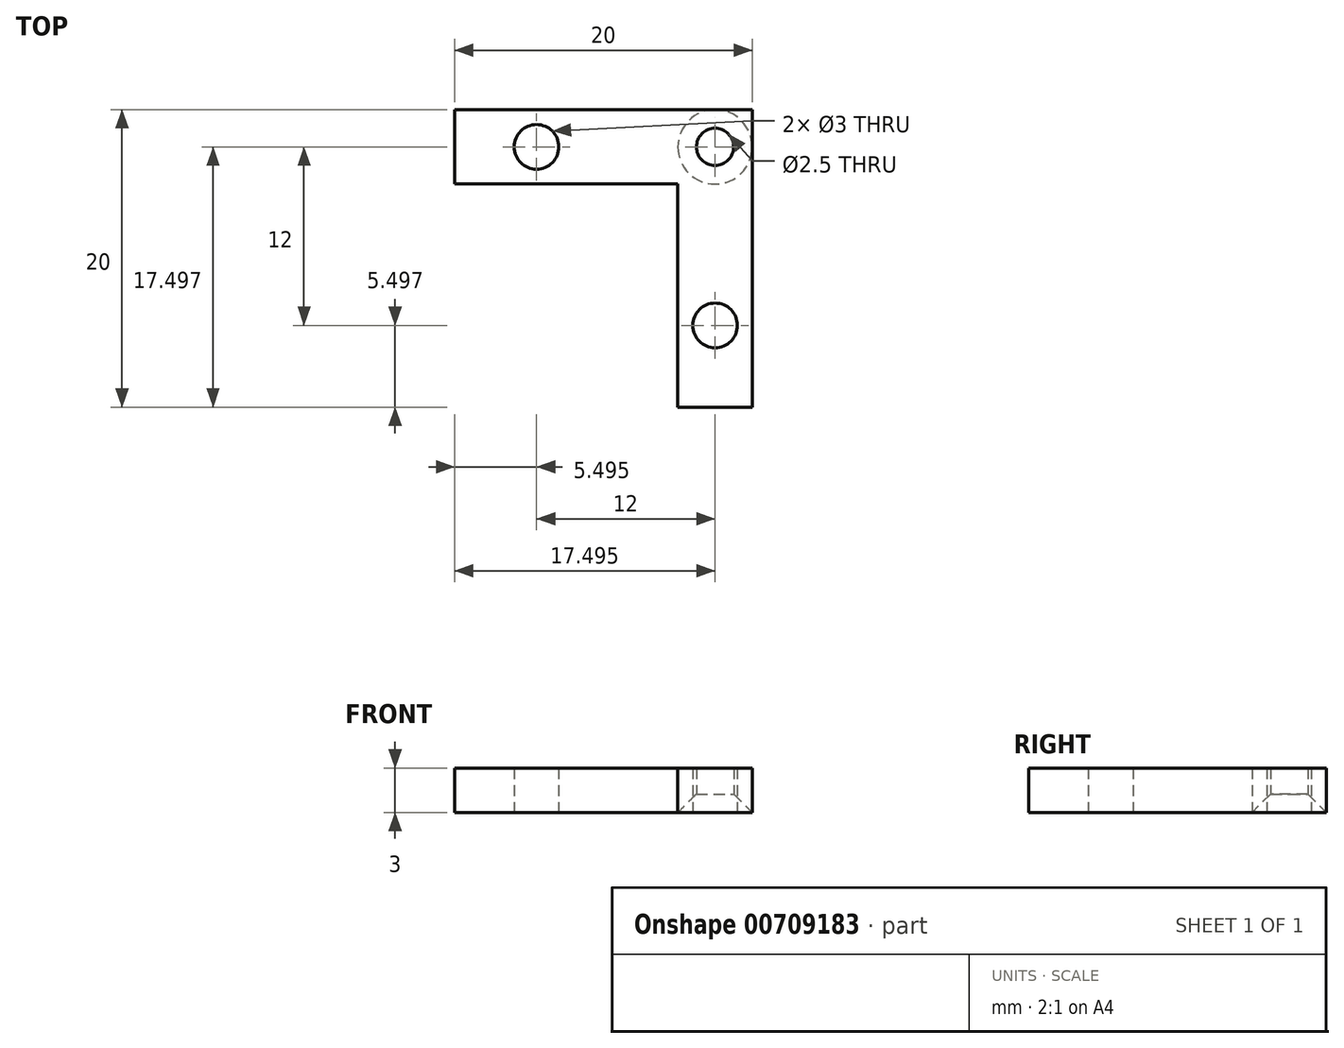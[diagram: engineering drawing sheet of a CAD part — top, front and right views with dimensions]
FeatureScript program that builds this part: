
annotation { "Feature Type Name" : "Feature", "Feature Type Description" : "" }
export const myFeature = defineFeature(function(context is Context, id is Id, definition is map)
    precondition{}
    {
        {
            var Q0;
            Q0=qCreatedBy(makeId("Top.planeOp"),FACE);
            var sketch = newSketch(context, id + "F0", { "sketchPlane" : qUnion([Q0])});
            skLineSegment(sketch, "E0.bottom", {"start": v(-24.65, 23.42) * mm, "end": v(-4.65, 23.42) * mm});
            skLineSegment(sketch, "E0.top", {"start": v(-24.65, 3.42) * mm, "end": v(-4.65, 3.42) * mm});
            skLineSegment(sketch, "E0.left", {"start": v(-24.65, 23.42) * mm, "end": v(-24.65, 3.42) * mm});
            skLineSegment(sketch, "E0.right", {"start": v(-4.65, 23.42) * mm, "end": v(-4.65, 3.42) * mm});
            skLineSegment(sketch, "E1.bottom", {"start": v(-24.65, 3.42) * mm, "end": v(-9.65, 3.42) * mm});
            skLineSegment(sketch, "E1.top", {"start": v(-24.65, 18.42) * mm, "end": v(-9.65, 18.42) * mm});
            skLineSegment(sketch, "E1.left", {"start": v(-24.65, 3.42) * mm, "end": v(-24.65, 18.42) * mm});
            skLineSegment(sketch, "E1.right", {"start": v(-9.65, 3.42) * mm, "end": v(-9.65, 18.42) * mm});
            skLineSegment(sketch, "E2", {"start": v(-9.65, 18.42) * mm, "end": v(-4.65, 23.42) * mm});
            skPoint(sketch, "E3", {"position": v(-7.15, 20.92) * mm});
            skPoint(sketch, "E4", {"position": v(-19.15, 20.92) * mm});
            skPoint(sketch, "E5", {"position": v(-7.15, 8.92) * mm});
            skSolve(sketch);
        }
        {
            var Q0;
            {var subQ0=sQuery(id+"F0.wireOp",EDGE,"E0.bottom");Q0=makeQuery(id+"F0.imprint","IMPRINT",FACE,{"disambiguationData":[TD([[makeQuery(id+"F0.imprint","IMPRINT",EDGE,{"derivedFrom":subQ0}),-1.0]])]});}
            var Q1;
            {var subQ0=sQuery(id+"F0.wireOp",EDGE,"E0.right");Q1=makeQuery(id+"F0.imprint","IMPRINT",FACE,{"disambiguationData":[TD([[makeQuery(id+"F0.imprint","IMPRINT",EDGE,{"derivedFrom":subQ0}),-1.0]])]});}
            extrude(context, id + "F1", {"entities" : qUnion([Q0, Q1]), "depth" : 3 * mm, "offsetDistance" : 25 * mm});
        }
        {
            var Q0;
            Q0=sQuery(id+"F0.wireOp",VERTEX,"E5");
            var Q1;
            Q1=sQuery(id+"F0.wireOp",VERTEX,"E4");
            var Q2;
            Q2=makeQuery(id+"F1.opExtrude","SWEPT_BODY",BODY,{"disambiguationData":[OSD([sQuery(id+"F0.wireOp",EDGE,"E0.bottom"),sQuery(id+"F0.wireOp",EDGE,"E0.top"),sQuery(id+"F0.wireOp",EDGE,"E0.left"),sQuery(id+"F0.wireOp",EDGE,"E0.right"),sQuery(id+"F0.wireOp",EDGE,"E1.top"),sQuery(id+"F0.wireOp",EDGE,"E1.right")])]});
            hole(context, id + "F2", {"style" : HoleStyle.SIMPLE, "endStyle" : HoleEndStyle.THROUGH, "oppositeDirection" : true, "holeDiameter" : 3 * mm, "majorDiameter" : 5 * mm, "isTappedThrough" : true, "tappedDepth" : 12 * mm, "tapClearance" : 3, "locations" : qUnion([Q0, Q1]), "scope" : qUnion([Q2])});
        }
        {
            var Q0;
            Q0=sQuery(id+"F0.wireOp",VERTEX,"E3");
            var Q1;
            Q1=makeQuery(id+"F1.opExtrude","SWEPT_BODY",BODY,{"disambiguationData":[OSD([sQuery(id+"F0.wireOp",EDGE,"E0.bottom"),sQuery(id+"F0.wireOp",EDGE,"E0.top"),sQuery(id+"F0.wireOp",EDGE,"E0.left"),sQuery(id+"F0.wireOp",EDGE,"E0.right"),sQuery(id+"F0.wireOp",EDGE,"E1.top"),sQuery(id+"F0.wireOp",EDGE,"E1.right")])]});
            hole(context, id + "F3", {"style" : HoleStyle.C_SINK, "endStyle" : HoleEndStyle.THROUGH, "oppositeDirection" : true, "holeDiameter" : 2.5 * mm, "cSinkDiameter" : 5 * mm, "cSinkAngle" : 90 * degree, "majorDiameter" : 5 * mm, "isTappedThrough" : true, "tappedDepth" : 12 * mm, "tapClearance" : 3, "locations" : qUnion([Q0]), "scope" : qUnion([Q1])});
        }
    });
